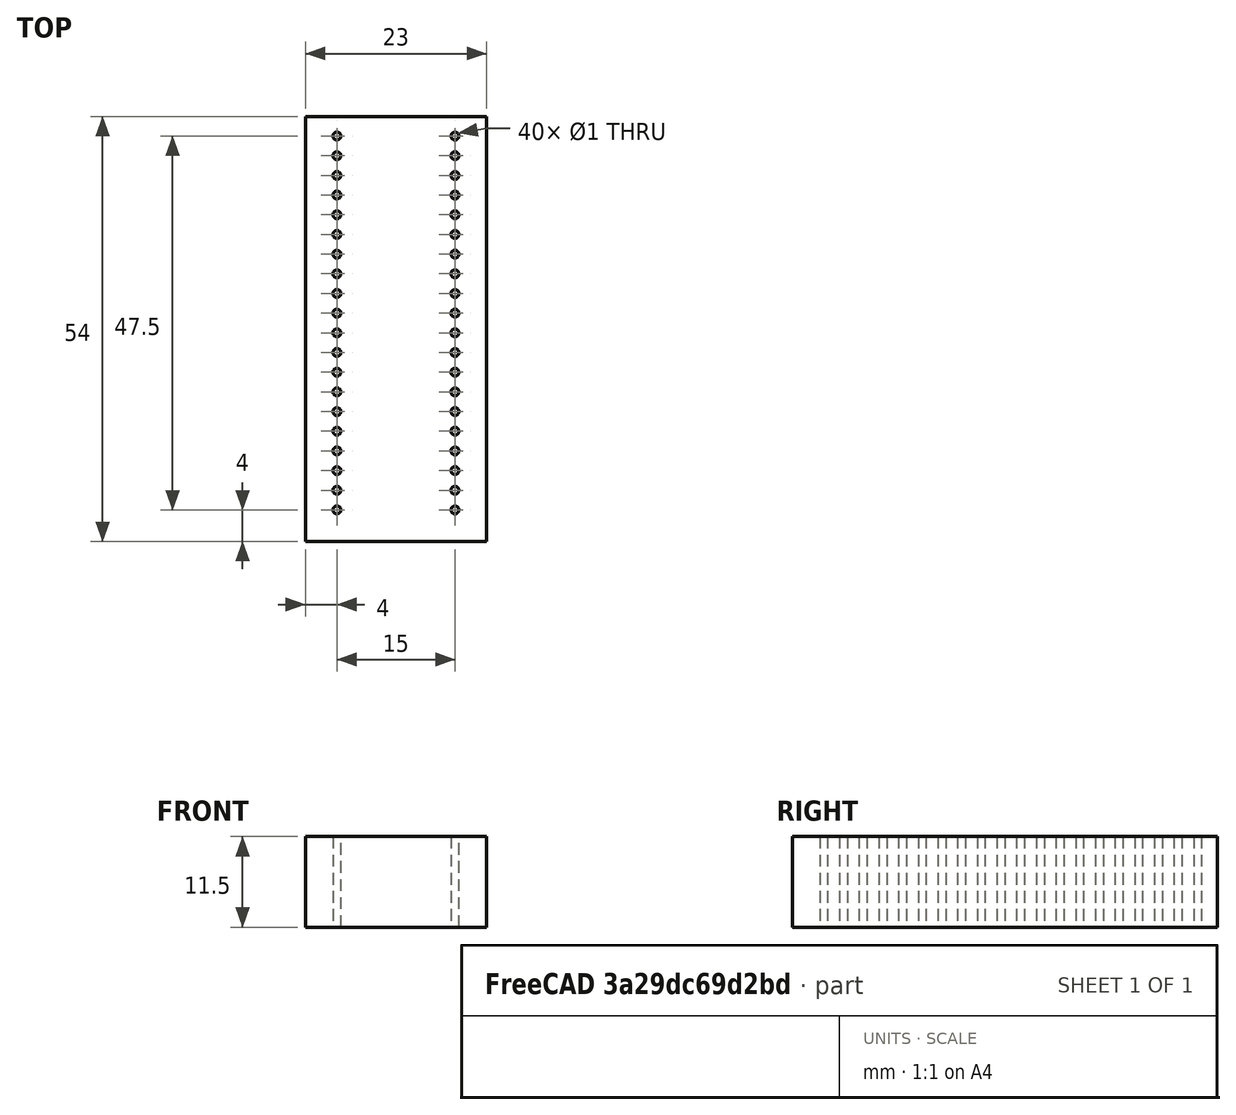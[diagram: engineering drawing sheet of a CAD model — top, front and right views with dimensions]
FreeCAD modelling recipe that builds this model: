
FCSTD DOCUMENT  (FreeCAD 0.19R24276 (Git))
Label: stm32f103
License: All rights reserved
LicenseURL: http://en.wikipedia.org/wiki/All_rights_reserved
objects: Sketcher::SketchObject×1, PartDesign::Pad×1, PartDesign::Body×1
note: 4 computed .brp shape members not serialized (recipe doc carries the construction recipe); baked Part::Feature solids carry a one-line shape summary decoded from their .brp

FEATURE [Sketcher::SketchObject] Sketch
  FullyConstrained = false
  MapMode = 5
  Support = -> [XY_Plane]
  sketch-geometry (45):
    g0: LineSegment StartX=0 StartY=0 StartZ=0 EndX=23 EndY=0 EndZ=0
    g1: LineSegment StartX=23 StartY=0 StartZ=0 EndX=23 EndY=-54 EndZ=0
    g2: LineSegment StartX=23 StartY=-54 StartZ=0 EndX=0 EndY=-54 EndZ=0
    g3: LineSegment StartX=0 StartY=-54 StartZ=0 EndX=0 EndY=0 EndZ=0
    g4: Circle CenterX=4 CenterY=-2.5 CenterZ=0 NormalX=0 NormalY=0 NormalZ=1 AngleXU=0 Radius=0.5
    g5: Circle CenterX=19 CenterY=-2.5 CenterZ=0 NormalX=0 NormalY=0 NormalZ=1 AngleXU=0 Radius=0.5
    g6: Circle CenterX=4 CenterY=-5 CenterZ=0 NormalX=0 NormalY=0 NormalZ=1 AngleXU=0 Radius=0.5
    g7: Circle CenterX=19 CenterY=-5 CenterZ=0 NormalX=0 NormalY=0 NormalZ=1 AngleXU=0 Radius=0.5
    g8: LineSegment StartX=11.5 StartY=0 StartZ=0 EndX=11.5 EndY=-2.5 EndZ=0
    g9: Circle CenterX=4 CenterY=-7.5 CenterZ=0 NormalX=0 NormalY=0 NormalZ=1 AngleXU=0 Radius=0.5
    g10: Circle CenterX=4 CenterY=-10 CenterZ=0 NormalX=0 NormalY=0 NormalZ=1 AngleXU=0 Radius=0.5
    g11: Circle CenterX=19 CenterY=-7.5 CenterZ=0 NormalX=0 NormalY=0 NormalZ=1 AngleXU=0 Radius=0.5
    g12: Circle CenterX=19 CenterY=-10 CenterZ=0 NormalX=0 NormalY=0 NormalZ=1 AngleXU=0 Radius=0.5
    g13: Circle CenterX=4 CenterY=-12.5 CenterZ=0 NormalX=0 NormalY=0 NormalZ=1 AngleXU=0 Radius=0.5
    g14: Circle CenterX=4 CenterY=-15 CenterZ=0 NormalX=0 NormalY=0 NormalZ=1 AngleXU=0 Radius=0.5
    g15: Circle CenterX=4 CenterY=-17.5 CenterZ=0 NormalX=0 NormalY=0 NormalZ=1 AngleXU=0 Radius=0.5
    g16: Circle CenterX=4 CenterY=-20 CenterZ=0 NormalX=0 NormalY=0 NormalZ=1 AngleXU=0 Radius=0.5
    g17: Circle CenterX=19 CenterY=-12.5 CenterZ=0 NormalX=0 NormalY=0 NormalZ=1 AngleXU=0 Radius=0.5
    g18: Circle CenterX=19 CenterY=-15 CenterZ=0 NormalX=0 NormalY=0 NormalZ=1 AngleXU=0 Radius=0.5
    g19: Circle CenterX=19 CenterY=-17.5 CenterZ=0 NormalX=0 NormalY=0 NormalZ=1 AngleXU=0 Radius=0.5
    g20: Circle CenterX=19 CenterY=-20 CenterZ=0 NormalX=0 NormalY=0 NormalZ=1 AngleXU=0 Radius=0.5
    g21: Circle CenterX=4 CenterY=-22.5 CenterZ=0 NormalX=0 NormalY=0 NormalZ=1 AngleXU=0 Radius=0.5
    g22: Circle CenterX=4 CenterY=-25 CenterZ=0 NormalX=0 NormalY=0 NormalZ=1 AngleXU=0 Radius=0.5
    g23: Circle CenterX=4 CenterY=-27.5 CenterZ=0 NormalX=0 NormalY=0 NormalZ=1 AngleXU=0 Radius=0.5
    g24: Circle CenterX=4 CenterY=-30 CenterZ=0 NormalX=0 NormalY=0 NormalZ=1 AngleXU=0 Radius=0.5
    g25: Circle CenterX=4 CenterY=-32.5 CenterZ=0 NormalX=0 NormalY=0 NormalZ=1 AngleXU=0 Radius=0.5
    g26: Circle CenterX=4 CenterY=-35 CenterZ=0 NormalX=0 NormalY=0 NormalZ=1 AngleXU=0 Radius=0.5
    g27: Circle CenterX=4 CenterY=-37.5 CenterZ=0 NormalX=0 NormalY=0 NormalZ=1 AngleXU=0 Radius=0.5
    g28: Circle CenterX=4 CenterY=-40 CenterZ=0 NormalX=0 NormalY=0 NormalZ=1 AngleXU=0 Radius=0.5
    g29: Circle CenterX=19 CenterY=-22.5 CenterZ=0 NormalX=0 NormalY=0 NormalZ=1 AngleXU=0 Radius=0.5
    g30: Circle CenterX=19 CenterY=-25 CenterZ=0 NormalX=0 NormalY=0 NormalZ=1 AngleXU=0 Radius=0.5
    g31: Circle CenterX=19 CenterY=-27.5 CenterZ=0 NormalX=0 NormalY=0 NormalZ=1 AngleXU=0 Radius=0.5
    g32: Circle CenterX=19 CenterY=-30 CenterZ=0 NormalX=0 NormalY=0 NormalZ=1 AngleXU=0 Radius=0.5
    g33: Circle CenterX=19 CenterY=-32.5 CenterZ=0 NormalX=0 NormalY=0 NormalZ=1 AngleXU=0 Radius=0.5
    g34: Circle CenterX=19 CenterY=-35 CenterZ=0 NormalX=0 NormalY=0 NormalZ=1 AngleXU=0 Radius=0.5
    g35: Circle CenterX=19 CenterY=-37.5 CenterZ=0 NormalX=0 NormalY=0 NormalZ=1 AngleXU=0 Radius=0.5
    g36: Circle CenterX=19 CenterY=-40 CenterZ=0 NormalX=0 NormalY=0 NormalZ=1 AngleXU=0 Radius=0.5
    g37: Circle CenterX=4 CenterY=-42.5 CenterZ=0 NormalX=0 NormalY=0 NormalZ=1 AngleXU=0 Radius=0.5
    g38: Circle CenterX=4 CenterY=-45 CenterZ=0 NormalX=0 NormalY=0 NormalZ=1 AngleXU=0 Radius=0.5
    g39: Circle CenterX=4 CenterY=-47.5 CenterZ=0 NormalX=0 NormalY=0 NormalZ=1 AngleXU=0 Radius=0.5
    g40: Circle CenterX=4 CenterY=-50 CenterZ=0 NormalX=0 NormalY=0 NormalZ=1 AngleXU=0 Radius=0.5
    g41: Circle CenterX=19 CenterY=-42.5 CenterZ=0 NormalX=0 NormalY=0 NormalZ=1 AngleXU=0 Radius=0.5
    g42: Circle CenterX=19 CenterY=-45 CenterZ=0 NormalX=0 NormalY=0 NormalZ=1 AngleXU=0 Radius=0.5
    g43: Circle CenterX=19 CenterY=-47.5 CenterZ=0 NormalX=0 NormalY=0 NormalZ=1 AngleXU=0 Radius=0.5
    g44: Circle CenterX=19 CenterY=-50 CenterZ=0 NormalX=0 NormalY=0 NormalZ=1 AngleXU=0 Radius=0.5
  constraints (132):
    c: Coincident(g0,g1)
    c: Coincident(g1,g2)
    c: Coincident(g2,g3)
    c: Coincident(g3,g0)
    c: Horizontal(g0)
    c: Horizontal(g2)
    c: Vertical(g1)
    c: Vertical(g3)
    c: Coincident(g0,g-1)
    c: DistanceX(g0,g0) = 23
    c: DistanceY(g1,g1) = 54
    c: Horizontal(g4,g5)
    c: Diameter(g4) = 1
    c: Equal(g4,g5)
    c: Horizontal(g6,g7)
    c: Equal(g4,g6) = 1
    c: Equal(g6,g7)
    c: Vertical(g7,g5)
    c: Vertical(g6,g4)
    c: DistanceX(g4,g5) = 15
    c: DistanceY(g7,g5) = 2.5
    c: Vertical(g8)
    c: Symmetric(g0,g0,g8)
    c: Symmetric(g4,g5,g8)
    c: DistanceY(g4,g0) = 2.5
    c: Horizontal(g9,g11)
    c: Equal(g4,g9) = 1
    c: Equal(g9,g11)
    c: Horizontal(g10,g12)
    c: Equal(g9,g10) = 1
    c: Equal(g10,g12)
    c: Vertical(g12,g11)
    c: Vertical(g10,g9)
    c: DistanceX(g9,g11) = 15
    c: DistanceY(g12,g11) = 2.5
    c: Vertical(g9,g6)
    c: DistanceY(g9,g6) = 2.5
    c: Horizontal(g13,g17)
    c: Equal(g4,g13) = 1
    c: Equal(g13,g17)
    c: Horizontal(g14,g18)
    c: Equal(g13,g14) = 1
    c: Equal(g14,g18)
    c: Vertical(g18,g17)
    c: Vertical(g14,g13)
    c: DistanceX(g13,g17) = 15
    c: DistanceY(g18,g17) = 2.5
    c: Horizontal(g15,g19)
    c: Equal(g13,g15) = 1
    c: Equal(g15,g19)
    c: Horizontal(g16,g20)
    c: Equal(g15,g16) = 1
    c: Equal(g16,g20)
    c: Vertical(g20,g19)
    c: Vertical(g16,g15)
    c: DistanceX(g15,g19) = 15
    c: DistanceY(g20,g19) = 2.5
    c: Vertical(g15,g14)
    c: DistanceY(g15,g14) = 2.5
    c: Vertical(g13,g10)
    c: DistanceY(g13,g10) = 2.5
    c: Horizontal(g21,g29)
    c: Equal(g4,g21) = 1
    c: Equal(g21,g29)
    c: Horizontal(g22,g30)
    c: Equal(g21,g22) = 1
    c: Equal(g22,g30)
    c: Vertical(g30,g29)
    c: Vertical(g22,g21)
    c: DistanceX(g21,g29) = 15
    c: DistanceY(g30,g29) = 2.5
    c: Horizontal(g23,g31)
    c: Equal(g21,g23) = 1
    c: Equal(g23,g31)
    c: Horizontal(g24,g32)
    c: Equal(g23,g24) = 1
    c: Equal(g24,g32)
    c: Vertical(g32,g31)
    c: Vertical(g24,g23)
    c: DistanceX(g23,g31) = 15
    c: DistanceY(g32,g31) = 2.5
    c: Vertical(g23,g22)
    c: DistanceY(g23,g22) = 2.5
    c: Horizontal(g25,g33)
    c: Equal(g21,g25) = 1
    c: Equal(g25,g33)
    c: Horizontal(g26,g34)
    c: Equal(g25,g26) = 1
    c: Equal(g26,g34)
    c: Vertical(g34,g33)
    c: Vertical(g26,g25)
    c: DistanceX(g25,g33) = 15
    c: DistanceY(g34,g33) = 2.5
    c: Horizontal(g27,g35)
    c: Equal(g25,g27) = 1
    c: Equal(g27,g35)
    c: Horizontal(g28,g36)
    c: Equal(g27,g28) = 1
    c: Equal(g28,g36)
    c: Vertical(g36,g35)
    c: Vertical(g28,g27)
    c: DistanceX(g27,g35) = 15
    c: DistanceY(g36,g35) = 2.5
    c: Vertical(g27,g26)
    c: DistanceY(g27,g26) = 2.5
    c: Vertical(g25,g24)
    c: DistanceY(g25,g24) = 2.5
    c: Vertical(g21,g16)
    c: DistanceY(g21,g16) = 2.5
    c: Horizontal(g37,g41)
    c: Equal(g37,g41)
    c: Horizontal(g38,g42)
    c: Equal(g37,g38) = 1
    c: Equal(g38,g42)
    c: Vertical(g42,g41)
    c: Vertical(g38,g37)
    c: DistanceX(g37,g41) = 15
    c: DistanceY(g42,g41) = 2.5
    c: Horizontal(g39,g43)
    c: Equal(g37,g39) = 1
    c: Equal(g39,g43)
    c: Horizontal(g40,g44)
    c: Equal(g39,g40) = 1
    c: Equal(g40,g44)
    c: Vertical(g44,g43)
    c: Vertical(g40,g39)
    c: DistanceX(g39,g43) = 15
    c: DistanceY(g44,g43) = 2.5
    c: Vertical(g39,g38)
    c: DistanceY(g39,g38) = 2.5
    c: Vertical(g37,g28)
    c: DistanceY(g37,g28) = 2.5
FEATURE [PartDesign::Pad] Pad
  Direction = (1,1,1)
  Length = 11.5
  Length2 = 100
  Profile = -> Sketch
  Type = 0
FEATURE [PartDesign::Body] Body
  Group = -> [Sketch,Pad]
  Origin = -> Origin
  Tip = -> Pad
